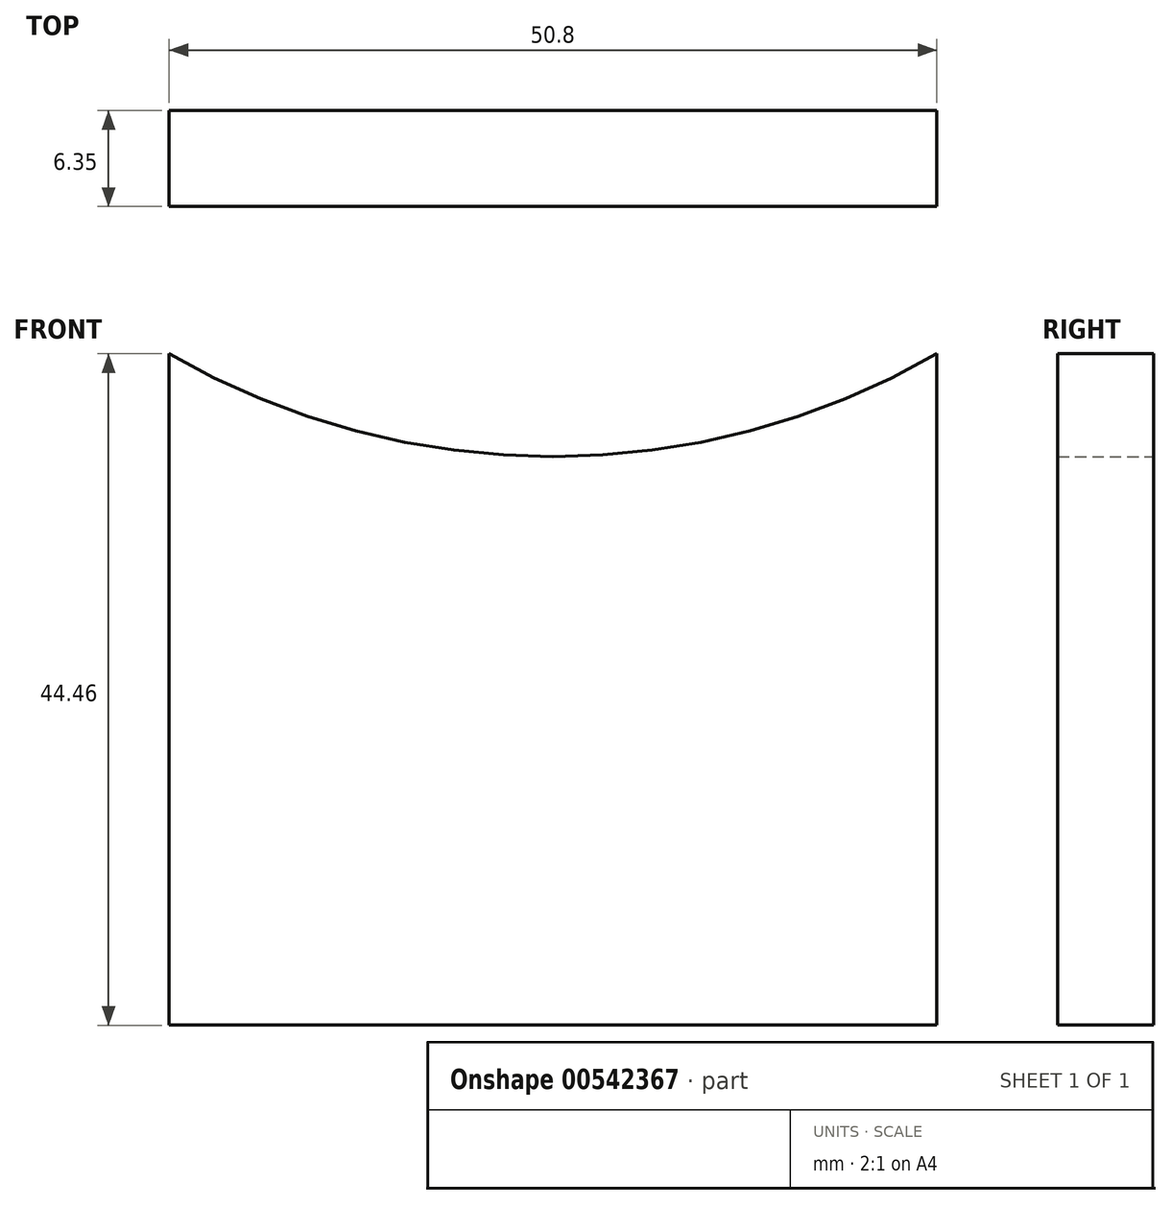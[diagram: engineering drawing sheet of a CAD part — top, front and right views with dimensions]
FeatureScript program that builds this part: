
annotation { "Feature Type Name" : "Feature", "Feature Type Description" : "" }
export const myFeature = defineFeature(function(context is Context, id is Id, definition is map)
    precondition{}
    {
        {
            var Q0;
            Q0=qCreatedBy(makeId("Front.planeOp"),FACE);
            var sketch = newSketch(context, id + "F0", { "sketchPlane" : qUnion([Q0])});
            skLineSegment(sketch, "E0.bottom", {"start": v(25.4, -22.23) * mm, "end": v(-25.4, -22.23) * mm});
            skLineSegment(sketch, "E0.left", {"start": v(25.4, -22.23) * mm, "end": v(25.4, 22.23) * mm});
            skLineSegment(sketch, "E0.right", {"start": v(-25.4, -22.23) * mm, "end": v(-25.4, 22.22) * mm});
            skPoint(sketch, "E0.middle", {"position": v(0, 0) * mm});
            skArc(sketch, "E1", {"start": v(-25.4, 22.22) * mm, "mid": v(0, 15.42) * mm, "end": v(25.4, 22.23) * mm});
            skSolve(sketch);
        }
        {
            var Q0;
            Q0=makeQuery(id+"F0.imprint","IMPRINT",FACE,{"disambiguationData":[TD([[makeQuery(id+"F0.imprint","IMPRINT",EDGE,{"derivedFrom":sQuery(id+"F0.wireOp",EDGE,"E0.bottom")}),-1.0]])]});
            extrude(context, id + "F1", {"entities" : qUnion([Q0]), "depth" : 6.35 * mm, "offsetDistance" : 25.4 * mm});
        }
    });
